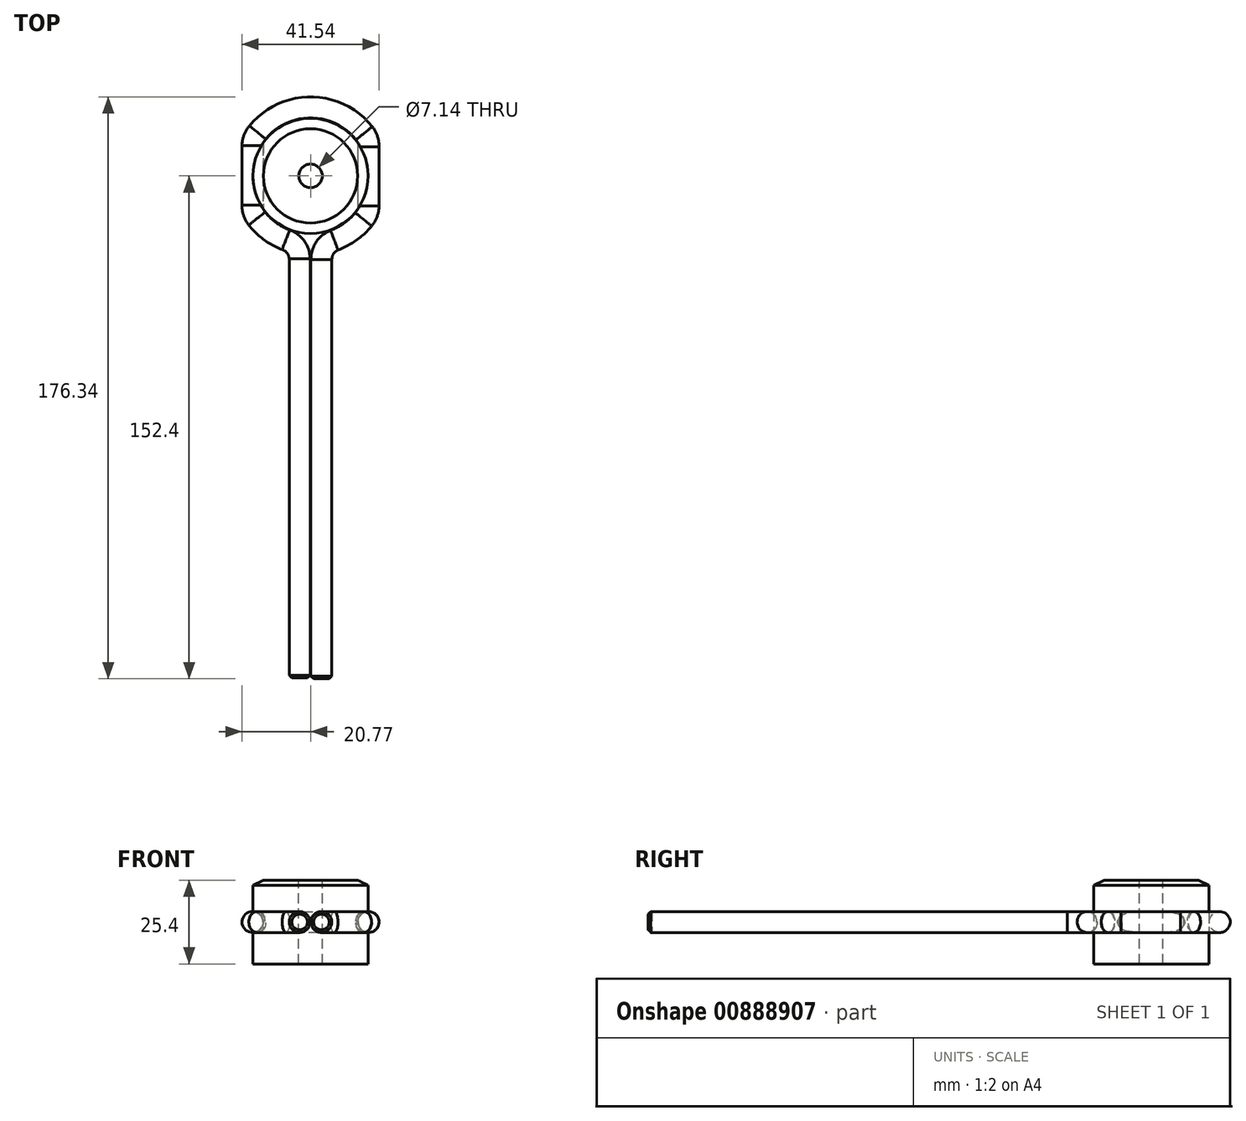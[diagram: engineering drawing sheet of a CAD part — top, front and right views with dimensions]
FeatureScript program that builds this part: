
annotation { "Feature Type Name" : "Feature", "Feature Type Description" : "" }
export const myFeature = defineFeature(function(context is Context, id is Id, definition is map)
    precondition{}
    {
        {
            var Q0;
            Q0=qCreatedBy(makeId("Top.planeOp"),FACE);
            var sketch = newSketch(context, id + "F0", { "sketchPlane" : qUnion([Q0])});
            skCircle(sketch, "E0", {"center": v(0, 0) * mm, "radius": 17.46 * mm});
            skSolve(sketch);
        }
        {
            var Q0;
            Q0=makeQuery(id+"F0.imprint","IMPRINT",FACE,{"disambiguationData":[TD([[makeQuery(id+"F0.imprint","IMPRINT",EDGE,{"derivedFrom":sQuery(id+"F0.wireOp",EDGE,"E0")}),1.0]])]});
            extrude(context, id + "F1", {"entities" : qUnion([Q0]), "depth" : 25.4 * mm, "offsetDistance" : 25.4 * mm});
        }
        {
            var Q0;
            Q0=makeQuery(id+"F1.opExtrude","CAP_FACE",FACE,{"disambiguationData":[OSD([sQuery(id+"F0.wireOp",EDGE,"E0")])],"isStart":false});
            var sketch = newSketch(context, id + "F2", { "sketchPlane" : qUnion([Q0])});
            skCircle(sketch, "E1", {"center": v(0, 0) * mm, "radius": 3.57 * mm});
            skSolve(sketch);
        }
        {
            var Q0;
            Q0 = qSketchRegion(id + "F2", true);
            extrude(context, id + "F3", {"entities" : qUnion([Q0]), "operationType" : NewBodyOperationType.REMOVE, "oppositeDirection" : true, "depth" : 25.4 * mm, "offsetDistance" : 25.4 * mm});
        }
        {
            var Q0;
            Q0=makeQuery(id+"F1.opExtrude","CAP_EDGE",EDGE,{"disambiguationData":[OSD([sQuery(id+"F0.wireOp",EDGE,"E0")])],"isStart":false});
            chamfer(context, id + "F4", {"entities" : qUnion([Q0]), "chamferType" : ChamferType.TWO_OFFSETS, "width1" : 1.59 * mm, "oppositeDirection" : true, "width2" : 3.17 * mm, "tangentPropagation" : true});
        }
        {
            var Q0;
            Q0=qCreatedBy(makeId("Front.planeOp"),FACE);
            var sketch = newSketch(context, id + "F5", { "sketchPlane" : qUnion([Q0])});
            skCircle(sketch, "E2", {"center": v(-17.46, 12.7) * mm, "radius": 3.18 * mm});
            skCircle(sketch, "E3", {"center": v(17.46, 12.7) * mm, "radius": 3.18 * mm});
            skSolve(sketch);
        }
        {
            var Q0;
            Q0 = qSketchRegion(id + "F5", true);
            extrude(context, id + "F6", {"entities" : qUnion([Q0]), "operationType" : NewBodyOperationType.REMOVE, "oppositeDirection" : true, "depth" : 25.4 * mm, "offsetDistance" : 25.4 * mm, "hasSecondDirection" : true, "secondDirectionOppositeDirection" : false, "secondDirectionDepth" : 25.4 * mm});
        }
        {
            var Q0;
            Q0=qCreatedBy(makeId("Top.planeOp"),FACE);
            cPlane(context, id + "F7", {"entities" : qUnion([Q0]), "cplaneType" : CPlaneType.OFFSET, "offset" : 12.7 * mm, "width" : 152.4 * mm, "height" : 152.4 * mm});
        }
        {
            var Q0;
            Q0=qCreatedBy(id+"F7.planeOp",FACE);
            var sketch = newSketch(context, id + "F8", { "sketchPlane" : qUnion([Q0])});
            skArc(sketch, "E4", {"start": v(-16.05, -12.97) * mm, "mid": v(-12.1, -16.73) * mm, "end": v(-7.28, -19.3) * mm});
            skLineSegment(sketch, "E5", {"start": v(-17.46, -8.98) * mm, "end": v(-17.46, 8.98) * mm});
            skLineSegment(sketch, "E6", {"start": v(17.46, -8.98) * mm, "end": v(17.46, 8.98) * mm});
            skArc(sketch, "E7.trimOffspring", {"start": v(16.05, 12.97) * mm, "mid": v(0, 20.64) * mm, "end": v(-16.05, 12.97) * mm});
            skPoint(sketch, "E8.orphan", {"position": v(-17.46, -21.17) * mm});
            skPoint(sketch, "E9.orphan", {"position": v(17.46, -21.17) * mm});
            skLineSegment(sketch, "E10", {"start": v(-3.17, -25.25) * mm, "end": v(-3.17, -25.4) * mm});
            skLineSegment(sketch, "E11", {"start": v(3.18, -25.25) * mm, "end": v(3.18, -25.4) * mm});
            skArc(sketch, "E12.trimOffspring", {"start": v(7.28, -19.3) * mm, "mid": v(12.1, -16.73) * mm, "end": v(16.05, -12.97) * mm});
            skArc(sketch, "E13", {"start": v(-16.05, 12.97) * mm, "mid": v(-17.1, 11.1) * mm, "end": v(-17.46, 8.98) * mm});
            skArc(sketch, "E14", {"start": v(-17.46, -8.98) * mm, "mid": v(-17.1, -11.1) * mm, "end": v(-16.05, -12.97) * mm});
            skArc(sketch, "E15", {"start": v(-3.17, -25.25) * mm, "mid": v(-4.3, -21.64) * mm, "end": v(-7.28, -19.3) * mm});
            skArc(sketch, "E16", {"start": v(7.28, -19.3) * mm, "mid": v(4.3, -21.64) * mm, "end": v(3.18, -25.25) * mm});
            skArc(sketch, "E17", {"start": v(16.05, -12.97) * mm, "mid": v(17.1, -11.1) * mm, "end": v(17.46, -8.98) * mm});
            skArc(sketch, "E18", {"start": v(17.46, 8.98) * mm, "mid": v(17.1, 11.1) * mm, "end": v(16.05, 12.97) * mm});
            skLineSegment(sketch, "E19", {"start": v(3.18, -25.25) * mm, "end": v(3.18, -152.25) * mm});
            skLineSegment(sketch, "E20", {"start": v(-3.17, -25.25) * mm, "end": v(-3.17, -152.25) * mm});
            skSolve(sketch);
        }
        {
            var Q0;
            Q0=qCreatedBy(makeId("Front.planeOp"),FACE);
            cPlane(context, id + "F9", {"entities" : qUnion([Q0]), "cplaneType" : CPlaneType.OFFSET, "offset" : 152.4 * mm, "width" : 152.4 * mm, "height" : 152.4 * mm});
        }
        {
            var Q0;
            Q0=qCreatedBy(id+"F9.planeOp",FACE);
            var sketch = newSketch(context, id + "F10", { "sketchPlane" : qUnion([Q0])});
            skCircle(sketch, "E21", {"center": v(3.3, 12.7) * mm, "radius": 3.18 * mm});
            skSolve(sketch);
        }
        {
            var Q0;
            Q0 = qSketchRegion(id + "F10", true);
            var Q1;
            Q1=sQuery(id+"F8.wireOp",EDGE,"E19");
            var Q2;
            Q2=sQuery(id+"F8.wireOp",EDGE,"E16");
            var Q3;
            Q3=sQuery(id+"F8.wireOp",EDGE,"E12.trimOffspring");
            var Q4;
            Q4=sQuery(id+"F8.wireOp",EDGE,"E17");
            var Q5;
            Q5=sQuery(id+"F8.wireOp",EDGE,"E6");
            var Q6;
            Q6=sQuery(id+"F8.wireOp",EDGE,"E18");
            var Q7;
            Q7=sQuery(id+"F8.wireOp",EDGE,"E7.trimOffspring");
            var Q8;
            Q8=sQuery(id+"F8.wireOp",EDGE,"E13");
            var Q9;
            Q9=sQuery(id+"F8.wireOp",EDGE,"E5");
            var Q10;
            Q10=sQuery(id+"F8.wireOp",EDGE,"E14");
            var Q11;
            Q11=sQuery(id+"F8.wireOp",EDGE,"E4");
            var Q12;
            Q12=sQuery(id+"F8.wireOp",EDGE,"E15");
            var Q13;
            Q13=sQuery(id+"F8.wireOp",EDGE,"E20");
            sweep(context, id + "F11", {"operationType" : NewBodyOperationType.ADD, "profiles" : qUnion([Q0]), "path" : qUnion([Q1, Q2, Q3, Q4, Q5, Q6, Q7, Q8, Q9, Q10, Q11, Q12, Q13])});
        }
        {
            var Q0;
            Q0=makeQuery(id+"F11.opSweep","CAP_FACE",FACE,{"disambiguationData":[OSD([sQuery(id+"F8.wireOp",VERTEX,"E20.end"),sQuery(id+"F10.wireOp",EDGE,"E21")])],"isStart":false});
            var Q1;
            Q1=makeQuery(id+"F11.opSweep","CAP_FACE",FACE,{"disambiguationData":[OSD([sQuery(id+"F8.wireOp",VERTEX,"E19.end"),sQuery(id+"F10.wireOp",EDGE,"E21")])],"isStart":true});
            chamfer(context, id + "F12", {"entities" : qUnion([Q0, Q1]), "width" : 0.8 * mm, "tangentPropagation" : true});
        }
    });
